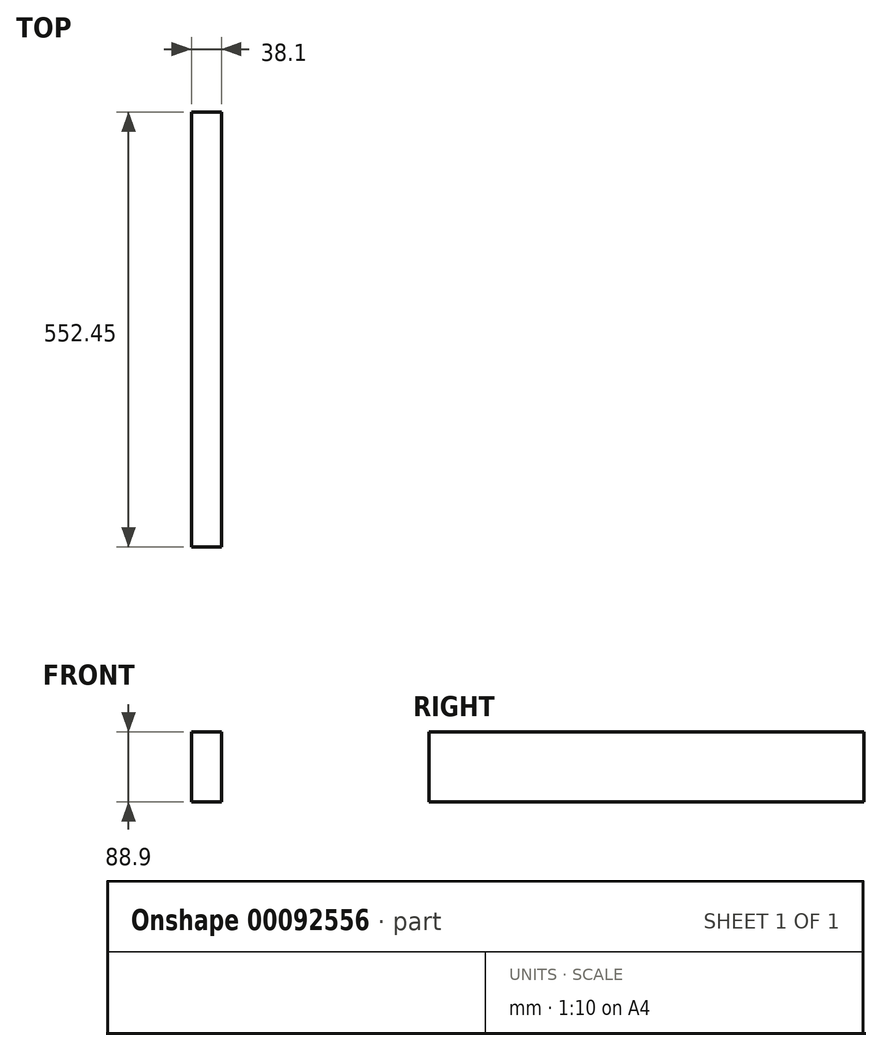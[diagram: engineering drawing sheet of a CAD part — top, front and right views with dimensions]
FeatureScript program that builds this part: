
annotation { "Feature Type Name" : "Feature", "Feature Type Description" : "" }
export const myFeature = defineFeature(function(context is Context, id is Id, definition is map)
    precondition{}
    {
        {
            var Q0;
            Q0=qCreatedBy(makeId("Right.planeOp"),FACE);
            var sketch = newSketch(context, id + "F0", { "sketchPlane" : qUnion([Q0])});
            skLineSegment(sketch, "E0.bottom", {"start": v(-296.83, 58.26) * mm, "end": v(255.62, 58.26) * mm});
            skLineSegment(sketch, "E0.top", {"start": v(-296.83, -30.64) * mm, "end": v(255.62, -30.64) * mm});
            skLineSegment(sketch, "E0.left", {"start": v(-296.83, 58.26) * mm, "end": v(-296.83, -30.64) * mm});
            skLineSegment(sketch, "E0.right", {"start": v(255.62, 58.26) * mm, "end": v(255.62, -30.64) * mm});
            skSolve(sketch);
        }
        {
            var Q0;
            Q0=makeQuery(id+"F0.imprint","IMPRINT",FACE,{"disambiguationData":[TD([[makeQuery(id+"F0.imprint","IMPRINT",EDGE,{"derivedFrom":sQuery(id+"F0.wireOp",EDGE,"E0.bottom")}),-1.0]])]});
            extrude(context, id + "F1", {"entities" : qUnion([Q0]), "depth" : 38.1 * mm});
        }
    });
